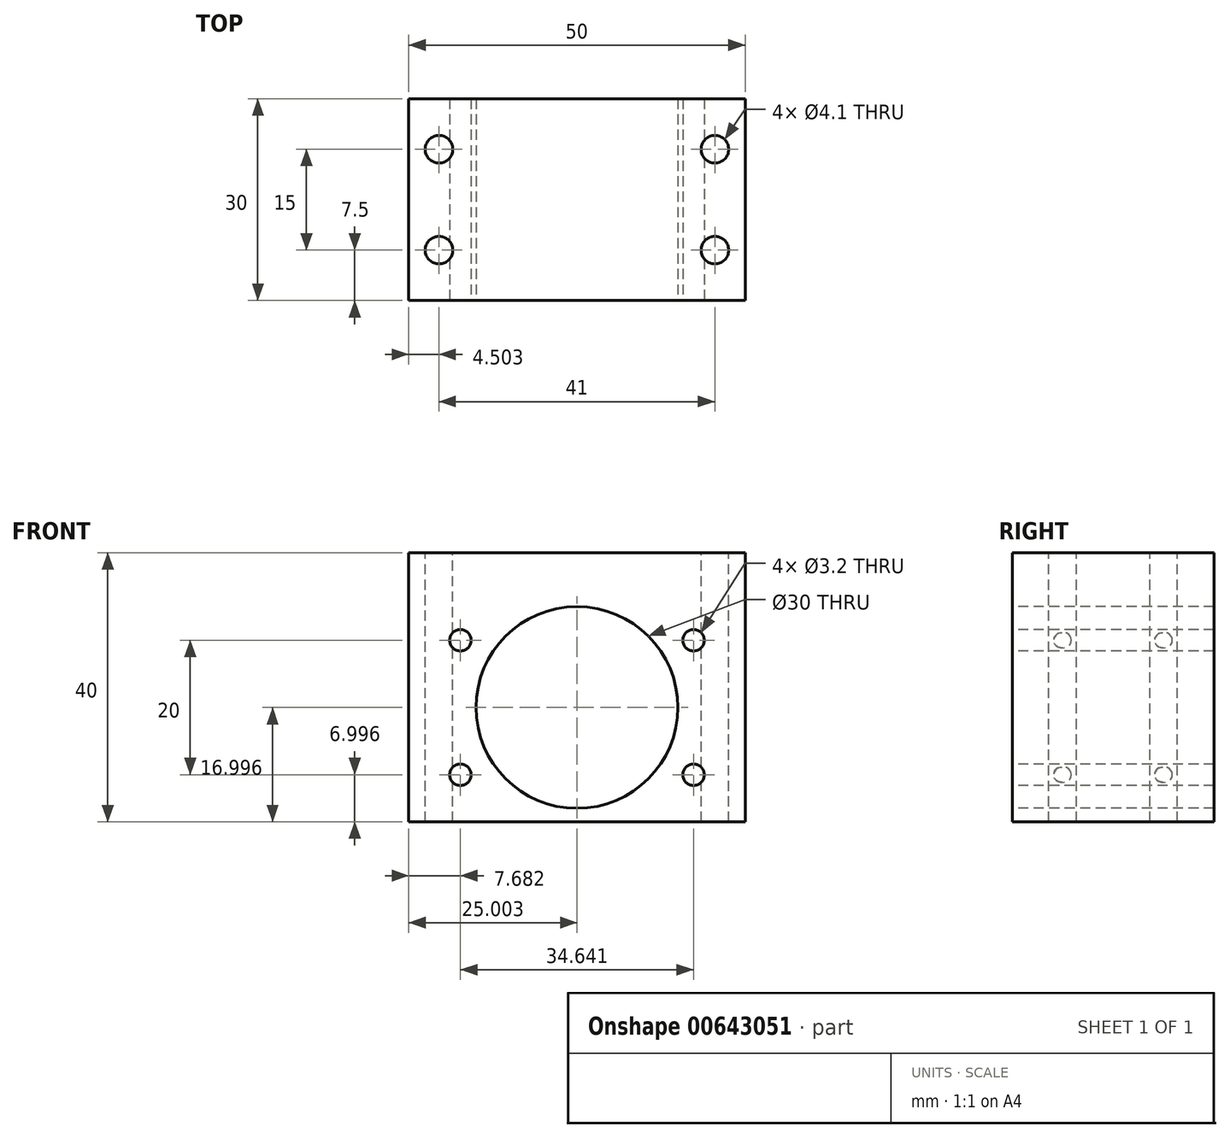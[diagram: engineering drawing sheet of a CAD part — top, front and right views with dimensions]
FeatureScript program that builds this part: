
annotation { "Feature Type Name" : "Feature", "Feature Type Description" : "" }
export const myFeature = defineFeature(function(context is Context, id is Id, definition is map)
    precondition{}
    {
        {
            var Q0;
            Q0=qCreatedBy(makeId("Front.planeOp"),FACE);
            var sketch = newSketch(context, id + "F0", { "sketchPlane" : qUnion([Q0])});
            skLineSegment(sketch, "E0.bottom", {"start": v(-21.59, 18.6) * mm, "end": v(28.41, 18.6) * mm});
            skLineSegment(sketch, "E0.top", {"start": v(-21.59, -21.4) * mm, "end": v(28.41, -21.4) * mm});
            skLineSegment(sketch, "E0.left", {"start": v(-21.59, 18.6) * mm, "end": v(-21.59, -21.4) * mm});
            skLineSegment(sketch, "E0.right", {"start": v(28.41, 18.6) * mm, "end": v(28.41, -21.4) * mm});
            skSolve(sketch);
        }
        {
            var Q0;
            Q0=makeQuery(id+"F0.imprint","IMPRINT",FACE,{"disambiguationData":[TD([[makeQuery(id+"F0.imprint","IMPRINT",EDGE,{"derivedFrom":sQuery(id+"F0.wireOp",EDGE,"E0.bottom")}),-1.0]])]});
            var Q1;
            Q1=qSketchRegion(id+"F2",true);
            extrude(context, id + "F1", {"entities" : qUnion([Q0, Q1]), "depth" : 30 * mm});
        }
        {
            var Q0;
            Q0=makeQuery(id+"F1.opExtrude","CAP_FACE",FACE,{"disambiguationData":[OSD([sQuery(id+"F0.wireOp",EDGE,"E0.bottom"),sQuery(id+"F0.wireOp",EDGE,"E0.top"),sQuery(id+"F0.wireOp",EDGE,"E0.left"),sQuery(id+"F0.wireOp",EDGE,"E0.right")])],"isStart":false});
            var sketch = newSketch(context, id + "F2", { "sketchPlane" : qUnion([Q0])});
            skLineSegment(sketch, "E1", {"start": v(3.41, 18.6) * mm, "end": v(3.41, -21.4) * mm, "construction": true});
            skLineSegment(sketch, "E2", {"start": v(-21.59, -4.4) * mm, "end": v(28.41, -4.4) * mm, "construction": true});
            skCircle(sketch, "E3", {"center": v(3.41, -4.4) * mm, "radius": 20 * mm, "construction": true});
            skCircle(sketch, "E4", {"center": v(3.41, -4.4) * mm, "radius": 15 * mm});
            skLineSegment(sketch, "E5", {"start": v(3.41, -4.4) * mm, "end": v(-31.63, 15.84) * mm, "construction": true});
            skPoint(sketch, "E6", {"position": v(-13.9, 5.6) * mm});
            skPoint(sketch, "E7.MirrorP", {"position": v(20.73, 5.6) * mm});
            skPoint(sketch, "E8", {"position": v(-16.59, -4.4) * mm});
            skPoint(sketch, "E9", {"position": v(23.41, -4.4) * mm});
            skPoint(sketch, "E10.MirrorP", {"position": v(-13.9, -14.4) * mm});
            skPoint(sketch, "E11.MirrorP", {"position": v(20.73, -14.4) * mm});
            skSolve(sketch);
        }
        {
            var Q0;
            Q0=makeQuery(id+"F2.imprint","IMPRINT",FACE,{"disambiguationData":[TD([[makeQuery(id+"F2.imprint","IMPRINT",EDGE,{"derivedFrom":sQuery(id+"F2.wireOp",EDGE,"E4")}),1.0]])]});
            extrude(context, id + "F3", {"entities" : qUnion([Q0]), "operationType" : NewBodyOperationType.REMOVE, "endBound" : BoundingType.THROUGH_ALL, "oppositeDirection" : true, "depth" : 25 * mm});
        }
        {
            var Q0;
            Q0=sQuery(id+"F2.wireOp",VERTEX,"E10.MirrorP");
            var Q1;
            Q1=sQuery(id+"F2.wireOp",VERTEX,"E6");
            var Q2;
            Q2=sQuery(id+"F2.wireOp",VERTEX,"E7.MirrorP");
            var Q3;
            Q3=sQuery(id+"F2.wireOp",VERTEX,"E11.MirrorP");
            var Q4;
            Q4=makeQuery(id+"F1.opExtrude","SWEPT_BODY",BODY,{"disambiguationData":[OSD([sQuery(id+"F0.wireOp",EDGE,"E0.bottom"),sQuery(id+"F0.wireOp",EDGE,"E0.top"),sQuery(id+"F0.wireOp",EDGE,"E0.left"),sQuery(id+"F0.wireOp",EDGE,"E0.right")])]});
            hole(context, id + "F4", {"style" : HoleStyle.SIMPLE, "endStyle" : HoleEndStyle.THROUGH, "standardTappedOrClearance" : lookupTablePath({ "standard" : "ISO", "engagement" : "75%", "pitch" : "0.75 mm", "size" : "M4", "type" : "Tapped" }), "standardBlindInLast" : lookupTablePath({ "standard" : "ISO", "engagement" : "75%", "pitch" : "0.75 mm", "size" : "M4", "type" : "Tapped" }), "holeDiameter" : 3.2 * mm, "locations" : qUnion([Q0, Q1, Q2, Q3]), "scope" : qUnion([Q4]), "tappedDepth" : 12 * mm, "tapClearance" : 3});
        }
        {
            var Q0;
            Q0=makeQuery(id+"F1.opExtrude","SWEPT_FACE",FACE,{"disambiguationData":[OSD([sQuery(id+"F0.wireOp",EDGE,"E0.bottom")])]});
            var sketch = newSketch(context, id + "F5", { "sketchPlane" : qUnion([Q0])});
            skLineSegment(sketch, "E12", {"start": v(28.41, -15) * mm, "end": v(-21.59, -15) * mm, "construction": true});
            skLineSegment(sketch, "E13", {"start": v(23.91, -30) * mm, "end": v(23.91, 0) * mm, "construction": true});
            skLineSegment(sketch, "E14", {"start": v(3.41, -30) * mm, "end": v(3.41, 0) * mm, "construction": true});
            skLineSegment(sketch, "E15.MirrorCS", {"start": v(-17.09, -30) * mm, "end": v(-17.09, 0) * mm, "construction": true});
            skLineSegment(sketch, "E16", {"start": v(28.41, -22.5) * mm, "end": v(-21.59, -22.5) * mm, "construction": true});
            skLineSegment(sketch, "E17.MirrorCS", {"start": v(28.41, -7.5) * mm, "end": v(-21.59, -7.5) * mm, "construction": true});
            skPoint(sketch, "E18", {"position": v(23.91, -22.5) * mm});
            skPoint(sketch, "E19", {"position": v(23.91, -7.5) * mm});
            skPoint(sketch, "E20", {"position": v(-17.09, -7.5) * mm});
            skPoint(sketch, "E21", {"position": v(-17.09, -22.5) * mm});
            skSolve(sketch);
        }
        {
            var Q0;
            Q0=sQuery(id+"F5.wireOp",VERTEX,"E18");
            var Q1;
            Q1=sQuery(id+"F5.wireOp",VERTEX,"E19");
            var Q2;
            Q2=sQuery(id+"F5.wireOp",VERTEX,"E20");
            var Q3;
            Q3=sQuery(id+"F5.wireOp",VERTEX,"E21");
            var Q4;
            Q4=makeQuery(id+"F1.opExtrude","SWEPT_BODY",BODY,{"disambiguationData":[OSD([sQuery(id+"F0.wireOp",EDGE,"E0.bottom"),sQuery(id+"F0.wireOp",EDGE,"E0.top"),sQuery(id+"F0.wireOp",EDGE,"E0.left"),sQuery(id+"F0.wireOp",EDGE,"E0.right")])]});
            hole(context, id + "F6", {"style" : HoleStyle.SIMPLE, "endStyle" : HoleEndStyle.THROUGH, "standardTappedOrClearance" : lookupTablePath({ "standard" : "ISO", "engagement" : "75%", "pitch" : "0.9 mm", "size" : "M5", "type" : "Tapped" }), "standardBlindInLast" : lookupTablePath({ "standard" : "ISO", "engagement" : "75%", "pitch" : "0.9 mm", "size" : "M5", "type" : "Tapped" }), "holeDiameter" : 4.1 * mm, "locations" : qUnion([Q0, Q1, Q2, Q3]), "scope" : qUnion([Q4]), "isTappedThrough" : true, "showTappedDepth" : true});
        }
    });
